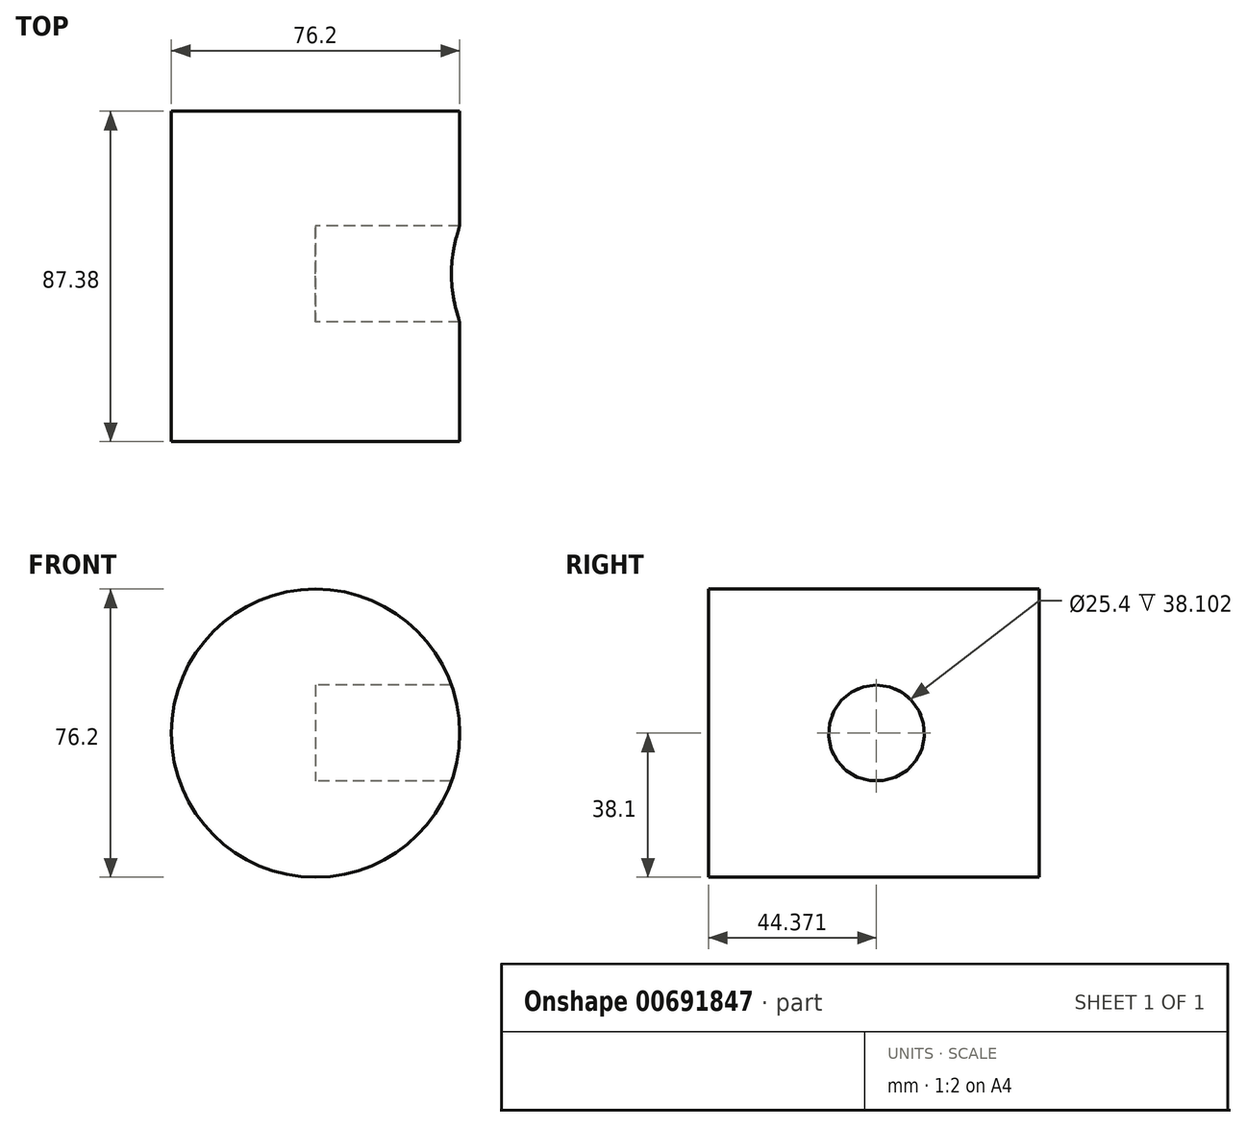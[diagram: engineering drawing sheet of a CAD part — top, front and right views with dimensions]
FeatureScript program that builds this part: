
annotation { "Feature Type Name" : "Feature", "Feature Type Description" : "" }
export const myFeature = defineFeature(function(context is Context, id is Id, definition is map)
    precondition{}
    {
        {
            var Q0;
            Q0=qCreatedBy(makeId("Front.planeOp"),FACE);
            var sketch = newSketch(context, id + "F0", { "sketchPlane" : qUnion([Q0])});
            skCircle(sketch, "E0", {"center": v(0, 0) * mm, "radius": 38.1 * mm});
            skLineSegment(sketch, "E1.top", {"start": v(-37.22, -43.68) * mm, "end": v(37.07, -43.68) * mm});
            skLineSegment(sketch, "E1.left", {"start": v(-37.22, -8.12) * mm, "end": v(-37.22, -43.68) * mm});
            skLineSegment(sketch, "E1.right", {"start": v(37.07, -10.03) * mm, "end": v(37.07, -43.68) * mm});
            skSolve(sketch);
        }
        {
            var Q0;
            Q0=makeQuery(id+"F0.imprint","IMPRINT",FACE,{"disambiguationData":[TD([[makeQuery(id+"F0.imprint","IMPRINT",EDGE,{"derivedFrom":sQuery(id+"F0.wireOp",EDGE,"E0")}),1.0]])]});
            extrude(context, id + "F1", {"entities" : qUnion([Q0]), "depth" : 87.38 * mm, "offsetDistance" : 25.4 * mm});
        }
        {
            var Q0;
            Q0=qCreatedBy(makeId("Right.planeOp"),FACE);
            var sketch = newSketch(context, id + "F2", { "sketchPlane" : qUnion([Q0])});
            skCircle(sketch, "E2", {"center": v(-43, 0) * mm, "radius": 21.87 * mm});
            skSolve(sketch);
        }
        {
            var Q0;
            Q0=sQuery(id+"F2.wireOp",VERTEX,"E2.center");
            var Q1;
            Q1=makeQuery(id+"F1.opExtrude","SWEPT_BODY",BODY,{"disambiguationData":[OSD([sQuery(id+"F0.wireOp",EDGE,"E0")])]});
            hole(context, id + "F3", {"style" : HoleStyle.SIMPLE, "endStyle" : HoleEndStyle.THROUGH, "oppositeDirection" : true, "holeDiameter" : 25.4 * mm, "majorDiameter" : 6.35 * mm, "isTappedThrough" : true, "tappedDepth" : 12.7 * mm, "tapClearance" : 3, "locations" : qUnion([Q0]), "scope" : qUnion([Q1])});
        }
    });
